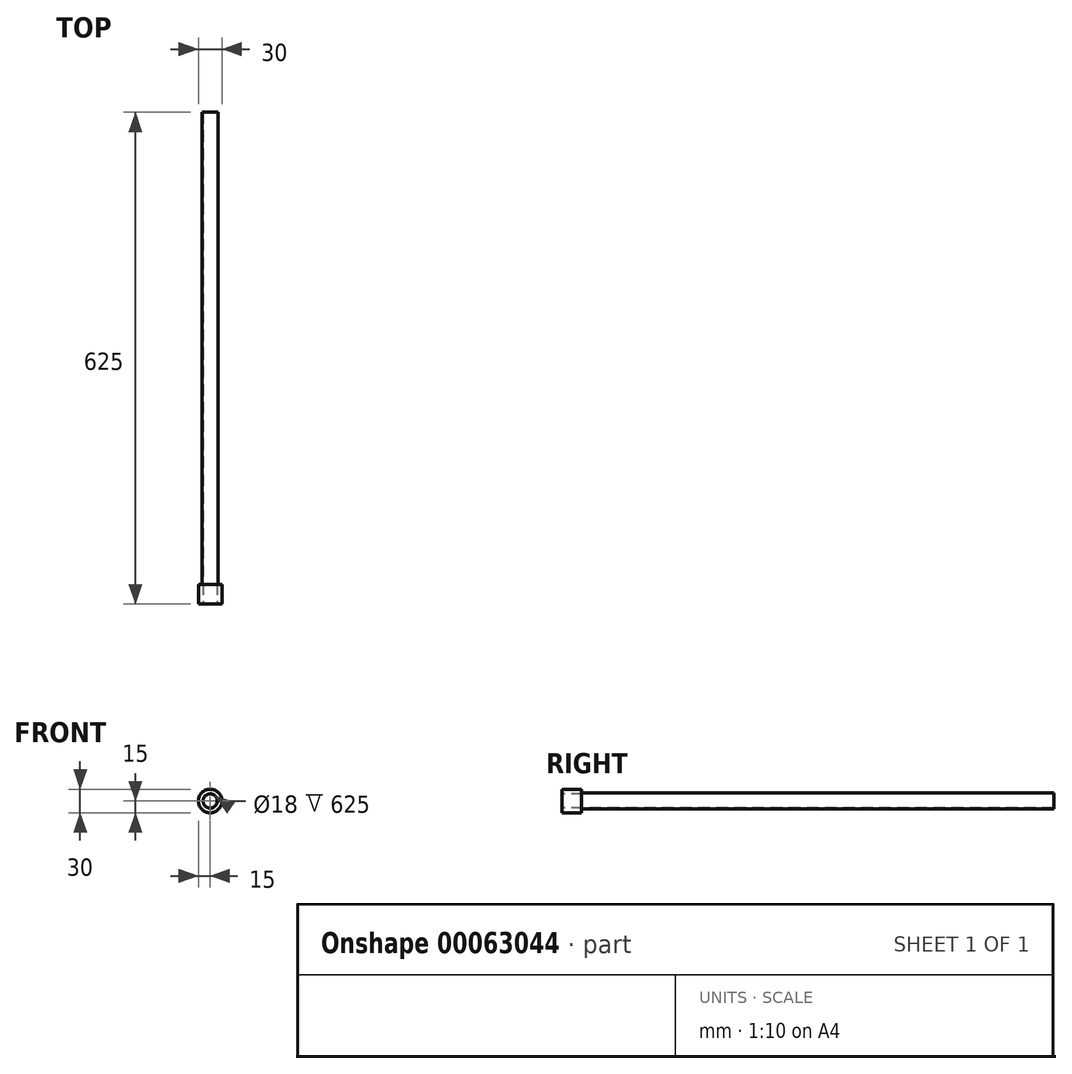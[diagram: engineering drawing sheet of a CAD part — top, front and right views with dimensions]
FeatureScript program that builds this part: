
annotation { "Feature Type Name" : "Feature", "Feature Type Description" : "" }
export const myFeature = defineFeature(function(context is Context, id is Id, definition is map)
    precondition{}
    {
        {
            var Q0;
            Q0=qCreatedBy(makeId("Front.planeOp"),FACE);
            var sketch = newSketch(context, id + "F0", { "sketchPlane" : qUnion([Q0])});
            skCircle(sketch, "E0", {"center": v(0, 0) * mm, "radius": 10 * mm});
            skSolve(sketch);
        }
        {
            var Q0;
            Q0=makeQuery(id+"F0.imprint","IMPRINT",FACE,{"disambiguationData":[TD([[makeQuery(id+"F0.imprint","IMPRINT",EDGE,{"derivedFrom":sQuery(id+"F0.wireOp",EDGE,"E0")}),1.0]])]});
            extrude(context, id + "F1", {"entities" : qUnion([Q0]), "depth" : 600 * mm});
        }
        {
            var Q0;
            Q0=makeQuery(id+"F1.opExtrude","CAP_FACE",FACE,{"disambiguationData":[OSD([sQuery(id+"F0.wireOp",EDGE,"E0")])],"isStart":false});
            var sketch = newSketch(context, id + "F2", { "sketchPlane" : qUnion([Q0])});
            skCircle(sketch, "E1", {"center": v(0, 0) * mm, "radius": 15 * mm});
            skSolve(sketch);
        }
        {
            var Q0;
            Q0=makeQuery(id+"F2.imprint","IMPRINT",FACE,{"disambiguationData":[TD([[makeQuery(id+"F2.imprint","IMPRINT",EDGE,{"derivedFrom":makeQuery(id+"F1.opExtrude","CAP_EDGE",EDGE,{"disambiguationData":[OSD([sQuery(id+"F0.wireOp",EDGE,"E0")])],"isStart":false})}),1.0]])]});
            var Q1;
            Q1=makeQuery(id+"F2.imprint","IMPRINT",FACE,{"disambiguationData":[TD([[makeQuery(id+"F2.imprint","IMPRINT",EDGE,{"derivedFrom":sQuery(id+"F2.wireOp",EDGE,"E1")}),1.0]])]});
            extrude(context, id + "F3", {"entities" : qUnion([Q0, Q1]), "operationType" : NewBodyOperationType.ADD, "depth" : 25 * mm});
        }
        {
            var Q0;
            Q0=makeQuery(id+"F3.opExtrude","CAP_FACE",FACE,{"disambiguationData":[OSD([sQuery(id+"F2.wireOp",EDGE,"E1")])],"isStart":false});
            var sketch = newSketch(context, id + "F4", { "sketchPlane" : qUnion([Q0])});
            skCircle(sketch, "E2", {"center": v(0, 0) * mm, "radius": 9 * mm});
            skSolve(sketch);
        }
        {
            var Q0;
            Q0 = qSketchRegion(id + "F4", true);
            var Q1;
            Q1=makeQuery(id+"F4.imprint","IMPRINT",FACE,{"disambiguationData":[TD([[makeQuery(id+"F4.imprint","IMPRINT",EDGE,{"derivedFrom":sQuery(id+"F4.wireOp",EDGE,"E2")}),1.0]])]});
            extrude(context, id + "F5", {"entities" : qUnion([Q0, Q1]), "operationType" : NewBodyOperationType.REMOVE, "oppositeDirection" : true, "depth" : 700 * mm});
        }
    });
